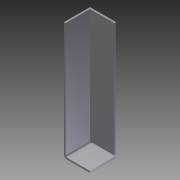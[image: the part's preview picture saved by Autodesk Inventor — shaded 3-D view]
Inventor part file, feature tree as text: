
AUTODESK INVENTOR PART (.ipt)
format: ipt  version: 2012 (Build 160160000, 160)  size: 90,624 bytes
history: native  units: in
note: dims shown in document units (in); Inventor stores cm internally (conversion verified against a paired STEP export)
features: extrude x2, fillet x2, sketch x1
ambient origin geometry x8: Origin, YZ Plane, XZ Plane, XY Plane, X Axis, Y Axis, Z Axis, Center Point
bodies: Solid1 (feature_tree)
feature tree (5):
  sketch  "Sketch1"  dims[d0=1.0in d1=4.5in d2=0.0625in d3=0.0625in d4=0.0438in d5=0.0625in d6=1.0in d7=0.0in d8=0.0625in d9=0.0in d10=0.0625in d11=0.125in]
  extrude  "Extrusion1"  Depth=4.5in
  extrude  "Extrusion2"  Depth=0.0625in
  fillet  "Fillet1"  Radius=0.0625in
  fillet  "Fillet2"  Radius=0.0438in
